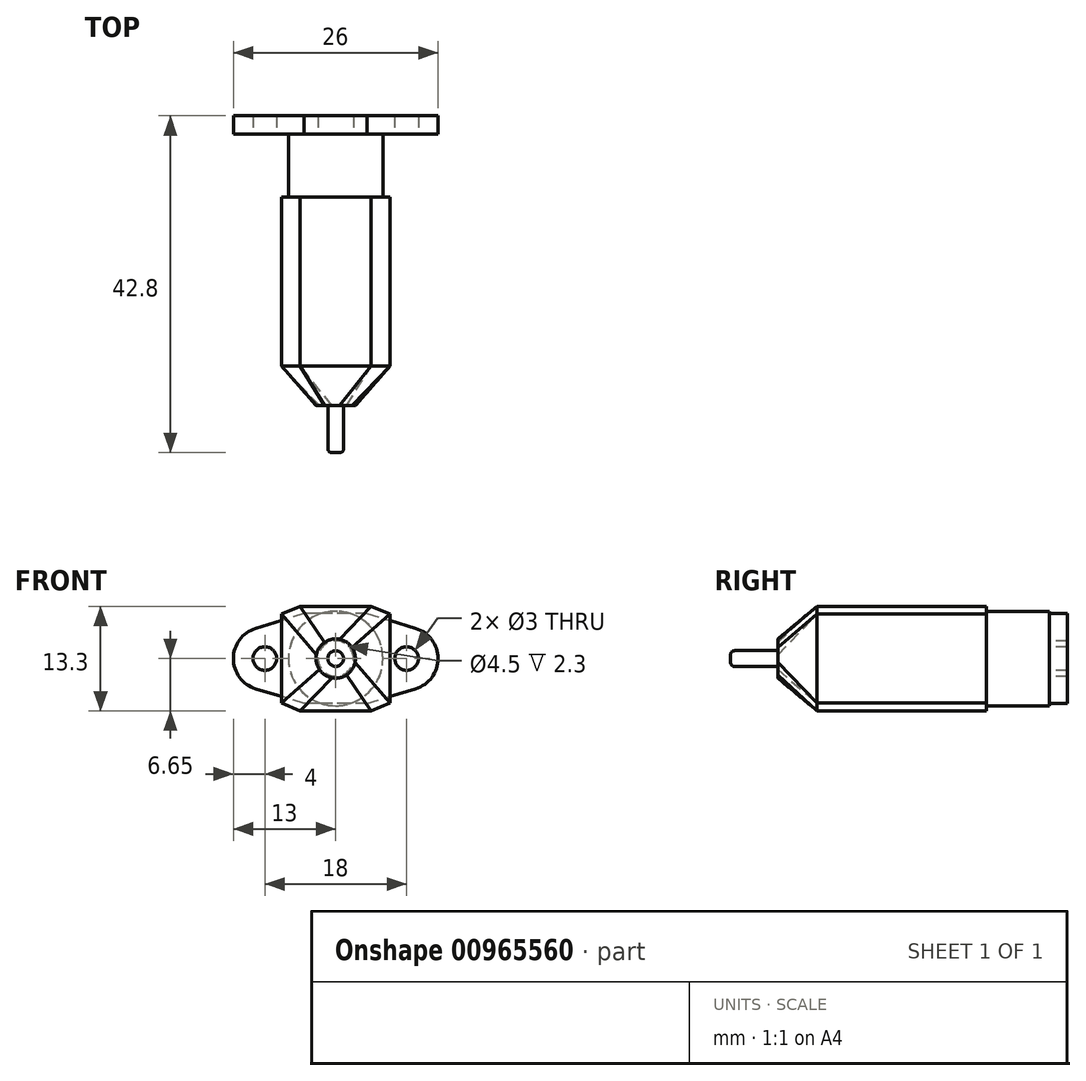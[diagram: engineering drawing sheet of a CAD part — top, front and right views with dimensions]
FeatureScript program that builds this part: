
annotation { "Feature Type Name" : "Feature", "Feature Type Description" : "" }
export const myFeature = defineFeature(function(context is Context, id is Id, definition is map)
    precondition{}
    {
        {
            var Q0;
            Q0=qCreatedBy(makeId("Front.planeOp"),FACE);
            var sketch = newSketch(context, id + "F0", { "sketchPlane" : qUnion([Q0])});
            skLineSegment(sketch, "E0.left", {"start": v(-6.9, 5.65) * mm, "end": v(-6.9, 5.65) * mm});
            skLineSegment(sketch, "E1", {"start": v(-4.5, 6.65) * mm, "end": v(4.5, 6.65) * mm});
            skLineSegment(sketch, "E2", {"start": v(6.9, 5.65) * mm, "end": v(6.9, -5.65) * mm});
            skLineSegment(sketch, "E3", {"start": v(-6.9, 5.65) * mm, "end": v(-6.9, -5.65) * mm});
            skLineSegment(sketch, "E4", {"start": v(-6.9, 5.65) * mm, "end": v(-4.5, 6.65) * mm});
            skLineSegment(sketch, "E5", {"start": v(4.5, 6.65) * mm, "end": v(6.9, 5.65) * mm});
            skLineSegment(sketch, "E6", {"start": v(-4.5, -6.65) * mm, "end": v(4.5, -6.65) * mm});
            skLineSegment(sketch, "E7", {"start": v(-6.9, -5.65) * mm, "end": v(-4.5, -6.65) * mm});
            skLineSegment(sketch, "E8", {"start": v(4.5, -6.65) * mm, "end": v(6.9, -5.65) * mm});
            skSolve(sketch);
        }
        {
            var Q0;
            Q0=makeQuery(id+"F0.imprint","IMPRINT",FACE,{"disambiguationData":[TD([[makeQuery(id+"F0.imprint","IMPRINT",EDGE,{"derivedFrom":sQuery(id+"F0.wireOp",EDGE,"E1")}),-1.0]])]});
            extrude(context, id + "F1", {"entities" : qUnion([Q0]), "depth" : 21.5 * mm, "offsetDistance" : 25 * mm});
        }
        {
            var Q0;
            Q0=qCreatedBy(makeId("Front.planeOp"),FACE);
            var sketch = newSketch(context, id + "F2", { "sketchPlane" : qUnion([Q0])});
            skCircle(sketch, "E9", {"center": v(0, 0) * mm, "radius": 6 * mm});
            skSolve(sketch);
        }
        {
            var Q0;
            Q0 = qSketchRegion(id + "F2", true);
            extrude(context, id + "F3", {"entities" : qUnion([Q0]), "operationType" : NewBodyOperationType.ADD, "oppositeDirection" : true, "depth" : 8 * mm, "offsetDistance" : 25 * mm});
        }
        {
            var Q0;
            Q0=makeQuery(id+"F1.opExtrude","CAP_FACE",FACE,{"disambiguationData":[OSD([sQuery(id+"F0.wireOp",EDGE,"E1"),sQuery(id+"F0.wireOp",EDGE,"E2"),sQuery(id+"F0.wireOp",EDGE,"E3"),sQuery(id+"F0.wireOp",EDGE,"E4"),sQuery(id+"F0.wireOp",EDGE,"E5"),sQuery(id+"F0.wireOp",EDGE,"E6"),sQuery(id+"F0.wireOp",EDGE,"E7"),sQuery(id+"F0.wireOp",EDGE,"E8")])],"isStart":false});
            cPlane(context, id + "F4", {"entities" : qUnion([Q0]), "cplaneType" : CPlaneType.OFFSET, "offset" : 5 * mm, "width" : 150 * mm, "height" : 150 * mm});
        }
        {
            var Q0;
            Q0=qCreatedBy(id+"F4.planeOp",FACE);
            var sketch = newSketch(context, id + "F5", { "sketchPlane" : qUnion([Q0])});
            skCircle(sketch, "E10", {"center": v(0, 0) * mm, "radius": 2.5 * mm});
            skSolve(sketch);
        }
        {
            var Q1;
            Q1=makeQuery(id+"F5.imprint","IMPRINT",FACE,{"disambiguationData":[TD([[makeQuery(id+"F5.imprint","IMPRINT",EDGE,{"derivedFrom":sQuery(id+"F5.wireOp",EDGE,"E10")}),1.0]])]});
            var Q2;
            Q2=makeQuery(id+"F1.opExtrude","CAP_FACE",FACE,{"disambiguationData":[OSD([sQuery(id+"F0.wireOp",EDGE,"E1"),sQuery(id+"F0.wireOp",EDGE,"E2"),sQuery(id+"F0.wireOp",EDGE,"E3"),sQuery(id+"F0.wireOp",EDGE,"E4"),sQuery(id+"F0.wireOp",EDGE,"E5"),sQuery(id+"F0.wireOp",EDGE,"E6"),sQuery(id+"F0.wireOp",EDGE,"E7"),sQuery(id+"F0.wireOp",EDGE,"E8")])],"isStart":false});
            var Q3;
            Q3=sQuery(id+"F5.wireOp",EDGE,"E10");
            loft(context, id + "F6", {"operationType" : NewBodyOperationType.ADD, "surfaceOperationType" : NewSurfaceOperationType.ADD, "sheetProfilesArray" : [{ "sheetProfileEntities" : qUnion([Q1]) }, { "sheetProfileEntities" : qUnion([Q2]) }], "wireProfilesArray" : [{ "wireProfileEntities" : qUnion([Q3]) }]});
        }
        {
            var Q0;
            Q0=makeQuery(id+"F6.opLoft","CAP_FACE",FACE,{"disambiguationData":[OSD([makeQuery(id+"F5.imprint","IMPRINT",FACE,{"disambiguationData":[TD([[makeQuery(id+"F5.imprint","IMPRINT",EDGE,{"derivedFrom":sQuery(id+"F5.wireOp",EDGE,"E10")}),1.0]])]})])],"isStart":true});
            var sketch = newSketch(context, id + "F7", { "sketchPlane" : qUnion([Q0])});
            skCircle(sketch, "E11", {"center": v(0, 0) * mm, "radius": 1 * mm});
            skSolve(sketch);
        }
        {
            var Q0;
            Q0 = qSketchRegion(id + "F7", true);
            extrude(context, id + "F8", {"entities" : qUnion([Q0]), "operationType" : NewBodyOperationType.ADD, "depth" : 6 * mm, "offsetDistance" : 25 * mm});
        }
        {
            var Q0;
            Q0=makeQuery(id+"F8.opExtrude","CAP_FACE",FACE,{"disambiguationData":[OSD([sQuery(id+"F7.wireOp",EDGE,"E11")])],"isStart":false});
            fillet(context, id + "F9", {"entities" : qUnion([Q0]), "radius" : 0.5 * mm, "tangentPropagation" : true, "allowEdgeOverflow" : false});
        }
        {
            var Q0;
            Q0=makeQuery(id+"F3.opExtrude","CAP_FACE",FACE,{"disambiguationData":[OSD([sQuery(id+"F2.wireOp",EDGE,"E9")])],"isStart":false});
            var sketch = newSketch(context, id + "F10", { "sketchPlane" : qUnion([Q0])});
            skCircle(sketch, "E12", {"center": v(0, 0) * mm, "radius": 2.25 * mm});
            skCircle(sketch, "E13", {"center": v(9, 0) * mm, "radius": 1.5 * mm});
            skCircle(sketch, "E14", {"center": v(-9, 0) * mm, "radius": 1.5 * mm});
            skArc(sketch, "E15", {"start": v(-10.16, 3.83) * mm, "mid": v(-13, 0) * mm, "end": v(-10.16, -3.83) * mm});
            skArc(sketch, "E16", {"start": v(10.16, -3.83) * mm, "mid": v(13, 0) * mm, "end": v(10.16, 3.83) * mm});
            skLineSegment(sketch, "E17.bottom", {"start": v(-4, 5.7) * mm, "end": v(4, 5.7) * mm});
            skLineSegment(sketch, "E17.top", {"start": v(-4, -5.7) * mm, "end": v(4, -5.7) * mm});
            skLineSegment(sketch, "E17.left", {"start": v(-4, 5.7) * mm, "end": v(-4, -5.7) * mm, "construction": true});
            skLineSegment(sketch, "E17.right", {"start": v(4, 5.7) * mm, "end": v(4, -5.7) * mm, "construction": true});
            skLineSegment(sketch, "E18", {"start": v(-4, 5.7) * mm, "end": v(-10.16, 3.83) * mm});
            skLineSegment(sketch, "E19", {"start": v(4, 5.7) * mm, "end": v(10.16, 3.83) * mm});
            skLineSegment(sketch, "E20", {"start": v(-4, -5.7) * mm, "end": v(-10.16, -3.83) * mm});
            skLineSegment(sketch, "E21", {"start": v(4, -5.7) * mm, "end": v(10.16, -3.83) * mm});
            skLineSegment(sketch, "E22", {"start": v(-10.16, 3.83) * mm, "end": v(-10.16, 3.83) * mm});
            skSolve(sketch);
        }
        {
            var Q0;
            Q0 = qSketchRegion(id + "F10", true);
            extrude(context, id + "F11", {"entities" : qUnion([Q0]), "operationType" : NewBodyOperationType.ADD, "depth" : 2.3 * mm, "offsetDistance" : 25 * mm});
        }
    });
